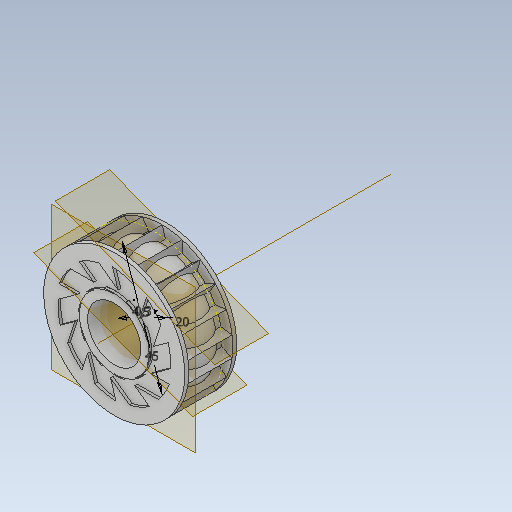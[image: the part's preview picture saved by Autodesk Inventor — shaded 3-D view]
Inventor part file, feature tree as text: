
AUTODESK INVENTOR PART (.ipt)
format: ipt  version: 2020 (Build 240168000, 168)  size: 535,040 bytes
history: native  units: mm
features: reference x80, sketch x10, extrude x9, other x8, plane x5, projected_geometry x3, pattern_circular x2, revolve x1, chamfer x1
ambient origin geometry x8: Origin, YZ Plane, XZ Plane, XY Plane, X Axis, Y Axis, Z Axis, Center Point
bodies: Solid1 (feature_tree)
feature tree (119):
  extrude  "Extrusion1"  Depth=45.0mm
  plane  "Work Plane3"
  revolve  "Revolution1"  [1 undecoded]
  sketch  "Sketch3"  dims[d7=1.5mm d8=1.5mm]
  plane  "Work Plane4"
  other  "Work Axis1"
  extrude  "Extrusion8"  Depth=1.5mm
  pattern_circular  "Circular Pattern3"  [2 undecoded]
  sketch  "Sketch6"  dims[d9=4.0mm]
  extrude  "Extrusion4"  [1 undecoded]
  extrude  "Extrusion5"  Depth=14.5mm TaperAngle=0.0deg
  extrude  "Extrusion6"  Depth=13.5mm TaperAngle=0.0deg
  extrude  "Extrusion7"  Depth=13.5mm
  pattern_circular  "Circular Pattern2"  [2 undecoded]
  sketch  "Sketch10"  dims[d12=2.0mm]
  plane  "Work Plane5"
  extrude  "Extrusion12"  Depth=13.5mm
  extrude  "Extrusion13"  Depth=13.5mm
  extrude  "Extrusion14"  TaperAngle=90.0deg  [1 undecoded]
  chamfer  "Chamfer4"  Distance=7.0mm
  sketch  "Sketch1"  dims[d0=0.3mm d1=45.0mm]
  reference  "Reference1"
  reference  "Reference2"
  reference  "Reference3"
  reference  "Reference4"
  reference  "Reference5"
  reference  "Reference6"
  reference  "Reference7"
  reference  "Reference8"
  reference  "Reference9"
  reference  "Reference10"
  reference  "Reference11"
  reference  "Reference12"
  reference  "Reference13"
  reference  "Reference14"
  reference  "Reference15"
  reference  "Reference16"
  reference  "Reference17"
  reference  "Reference18"
  reference  "Reference19"
  reference  "Reference20"
  reference  "Reference21"
  reference  "Reference22"
  reference  "Reference23"
  reference  "Reference24"
  reference  "Reference25"
  reference  "Reference26"
  reference  "Reference27"
  reference  "Reference28"
  reference  "Reference29"
  reference  "Reference30"
  reference  "Reference31"
  reference  "Reference32"
  reference  "Reference33"
  reference  "Reference34"
  reference  "Reference35"
  reference  "Reference36"
  reference  "Reference37"
  reference  "Reference38"
  reference  "Reference39"
  reference  "Reference40"
  reference  "Reference41"
  reference  "Reference42"
  reference  "Reference43"
  reference  "Reference44"
  reference  "Reference45"
  reference  "Reference46"
  reference  "Reference47"
  reference  "Reference48"
  reference  "Reference49"
  reference  "Reference50"
  reference  "Reference51"
  reference  "Reference52"
  reference  "Reference53"
  reference  "Reference54"
  reference  "Reference55"
  reference  "Reference56"
  reference  "Reference57"
  reference  "Reference58"
  reference  "Reference59"
  reference  "Reference60"
  reference  "Reference61"
  reference  "Reference62"
  reference  "Reference63"
  reference  "Reference64"
  reference  "Reference65"
  reference  "Reference66"
  reference  "Reference67"
  reference  "Reference68"
  reference  "Reference69"
  reference  "Reference70"
  reference  "Reference71"
  reference  "Reference72"
  reference  "Reference73"
  reference  "Reference74"
  reference  "Reference75"
  reference  "Reference76"
  reference  "Reference77"
  reference  "Reference78"
  reference  "Reference79"
  reference  "Reference80"
  plane  "Work Plane1"
  plane  "Work Plane2"
  sketch  "Sketch2"  dims[d2=20.0mm d3=10.5mm d4=9.0mm d5=0.0mm d6=0.0mm]
  projected_geometry  "Projected Loop1"
  sketch  "Sketch7"  dims[d10=2.0mm]
  projected_geometry  "Projected Loop2"
  sketch  "Sketch8"  dims[d11=2.0mm]
  sketch  "Sketch12"  dims[d13=90.0deg]
  sketch  "Sketch13"  dims[d14=4.0mm]
  sketch  "Sketch14"  dims[d15=1.25mm d16=1.25mm d17=-3.5mm d26=14.5mm d27=0.0mm d28=9.5mm d29=0.0mm d30=2.5mm d31=4.0mm d32=0.0mm d34=3.0mm d36=3.0mm d37=90.0deg d38=7.0mm d39=1.0mm d40=0.0mm d41=100.0mm d42=360.0deg d53=19.0mm d54=0.0mm d55=220.0mm d56=360.0deg d61=44.0mm d62=2.5mm d63=8.776542mm d65=12.283861mm d66=4.5mm d71=14.0mm d72=0.0mm d73=8.0mm d74=0.0mm d75=4.5mm d76=7.0mm d77=0.0mm d78=13.5mm d79=4.0mm d80=45.0deg]
  projected_geometry  "Projected Loop3"
  other  "<userpath>\Desktop\3d\scanning-robot\Assembly1.iam"
  other  "Assembly1.iam"
  other  "Tower Pro MG90S Micro servo:2"
  other  "Цилиндрическое зубчатое зацепление:5"
  other  "Цилиндрическое зубчатое зацепление2:1"
  other  "Assembly1"
  other  "base:1"
note: 7 required parameter values undecoded (feature->parameter linkage not recoverable at this tier; creation-order binding heuristic only, values carry confidence <= 0.55)